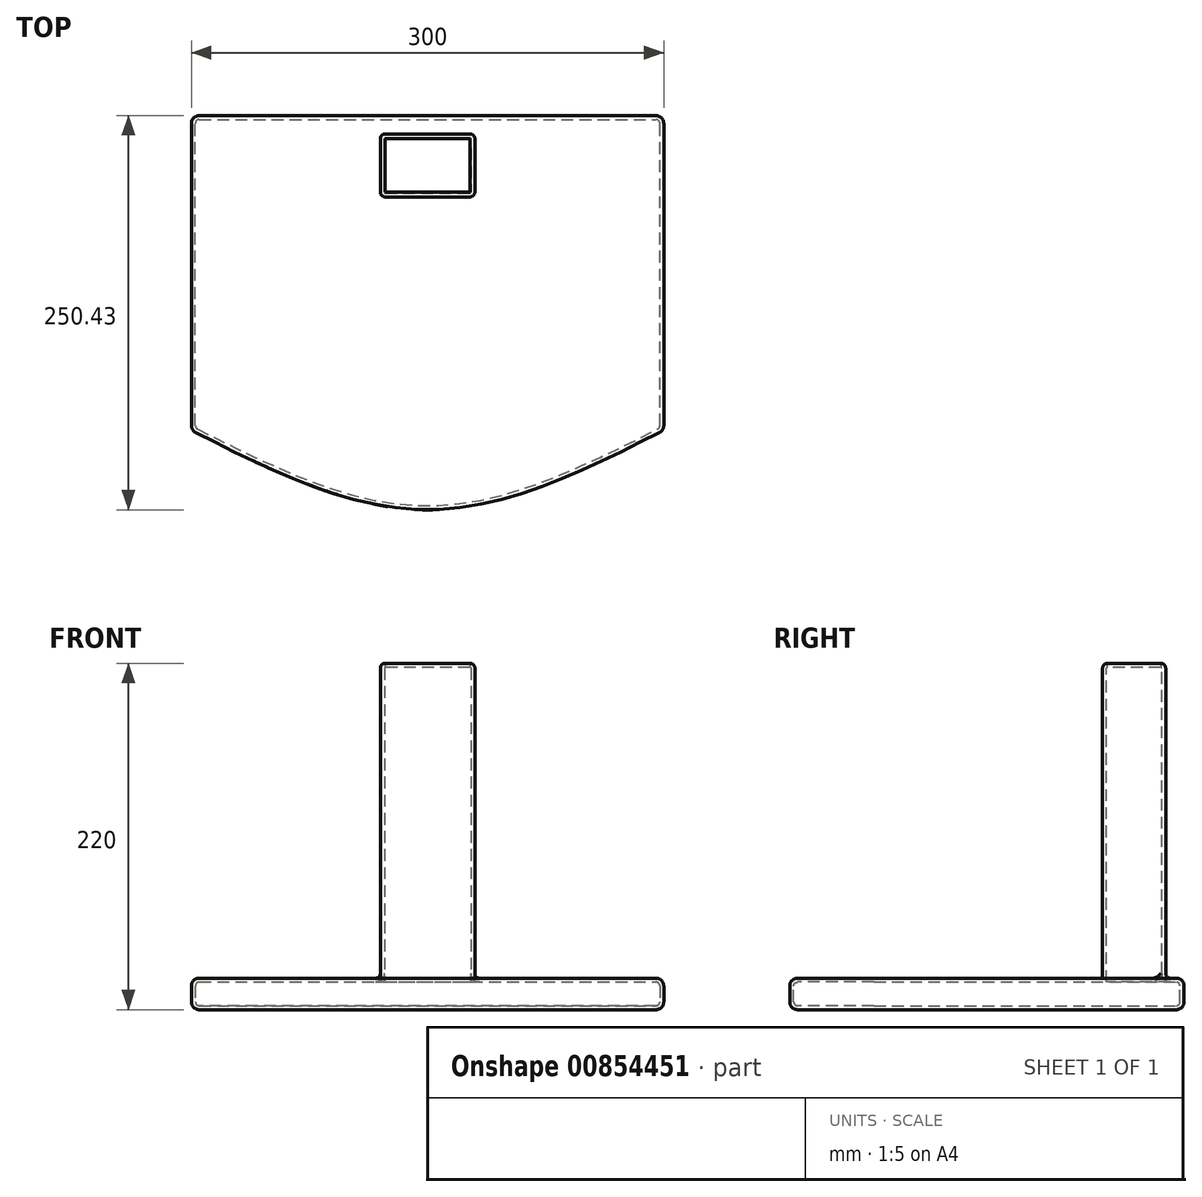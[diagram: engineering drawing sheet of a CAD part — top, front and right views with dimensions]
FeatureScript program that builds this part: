
annotation { "Feature Type Name" : "Feature", "Feature Type Description" : "" }
export const myFeature = defineFeature(function(context is Context, id is Id, definition is map)
    precondition{}
    {
        {
            var Q0;
            Q0=qCreatedBy(makeId("Top.planeOp"),FACE);
            var sketch = newSketch(context, id + "F0", { "sketchPlane" : qUnion([Q0])});
            skLineSegment(sketch, "E0.bottom", {"start": v(-150, 100) * mm, "end": v(150, 100) * mm});
            skLineSegment(sketch, "E0.left", {"start": v(-150, 100) * mm, "end": v(-150, -100) * mm});
            skLineSegment(sketch, "E0.right", {"start": v(150, 100) * mm, "end": v(150, -100) * mm});
            skFitSpline(sketch, "E1", {"points": [v(-150, -100) * mm, v(0, -150.43) * mm, v(150, -100) * mm], "startDerivative": vector(300, -151.28) * mm, "endDerivative": vector(300, 151.28) * mm});
            skSolve(sketch);
        }
        {
            var Q0;
            Q0=makeQuery(id+"F0.imprint","IMPRINT",FACE,{"disambiguationData":[TD([[makeQuery(id+"F0.imprint","IMPRINT",EDGE,{"derivedFrom":sQuery(id+"F0.wireOp",EDGE,"E0.bottom")}),-1.0]])]});
            extrude(context, id + "F1", {"entities" : qUnion([Q0]), "depth" : 20 * mm, "offsetDistance" : 25 * mm});
        }
        {
            var Q0;
            Q0=makeQuery(id+"F1.opExtrude","SWEPT_FACE",FACE,{"disambiguationData":[OSD([sQuery(id+"F0.wireOp",EDGE,"E0.left")])]});
            var Q1;
            Q1=makeQuery(id+"F1.opExtrude","SWEPT_FACE",FACE,{"disambiguationData":[OSD([sQuery(id+"F0.wireOp",EDGE,"E1")])]});
            var Q2;
            Q2=makeQuery(id+"F1.opExtrude","SWEPT_FACE",FACE,{"disambiguationData":[OSD([sQuery(id+"F0.wireOp",EDGE,"E0.right")])]});
            var Q3;
            Q3=makeQuery(id+"F1.opExtrude","SWEPT_FACE",FACE,{"disambiguationData":[OSD([sQuery(id+"F0.wireOp",EDGE,"E0.bottom")])]});
            fillet(context, id + "F2", {"entities" : qUnion([Q0, Q1, Q2, Q3]), "radius" : 5 * mm, "tangentPropagation" : true, "allowEdgeOverflow" : false});
        }
        {
            var Q0;
            Q0=makeQuery(id+"F1.opExtrude","CAP_FACE",FACE,{"disambiguationData":[OSD([sQuery(id+"F0.wireOp",EDGE,"E0.bottom"),sQuery(id+"F0.wireOp",EDGE,"E0.left"),sQuery(id+"F0.wireOp",EDGE,"E0.right"),sQuery(id+"F0.wireOp",EDGE,"E1")])],"isStart":false});
            var sketch = newSketch(context, id + "F3", { "sketchPlane" : qUnion([Q0])});
            skLineSegment(sketch, "E2.bottom", {"start": v(-30, 88.32) * mm, "end": v(30, 88.32) * mm});
            skLineSegment(sketch, "E2.top", {"start": v(-30, 48.32) * mm, "end": v(30, 48.32) * mm});
            skLineSegment(sketch, "E2.left", {"start": v(-30, 88.32) * mm, "end": v(-30, 48.32) * mm});
            skLineSegment(sketch, "E2.right", {"start": v(30, 88.32) * mm, "end": v(30, 48.32) * mm});
            skSolve(sketch);
        }
        {
            var Q0;
            Q0=makeQuery(id+"F3.imprint","IMPRINT",FACE,{"disambiguationData":[TD([[makeQuery(id+"F3.imprint","IMPRINT",EDGE,{"derivedFrom":sQuery(id+"F3.wireOp",EDGE,"E2.bottom")}),-1.0]])]});
            extrude(context, id + "F4", {"entities" : qUnion([Q0]), "operationType" : NewBodyOperationType.ADD, "depth" : 200 * mm, "offsetDistance" : 25 * mm});
        }
        {
            var Q0;
            Q0=makeQuery(id+"F4.opExtrude","CAP_EDGE",EDGE,{"disambiguationData":[OSD([sQuery(id+"F3.wireOp",EDGE,"E2.top")])],"isStart":false});
            var Q1;
            Q1=makeQuery(id+"F4.opExtrude","CAP_EDGE",EDGE,{"disambiguationData":[OSD([sQuery(id+"F3.wireOp",EDGE,"E2.right")])],"isStart":false});
            var Q2;
            Q2=makeQuery(id+"F4.opExtrude","SWEPT_EDGE",EDGE,{"disambiguationData":[OSD([sQuery(id+"F3.wireOp",EDGE,"E2.bottom"),sQuery(id+"F3.wireOp",EDGE,"E2.right")])]});
            var Q3;
            Q3=makeQuery(id+"F4.opExtrude","SWEPT_FACE",FACE,{"disambiguationData":[OSD([sQuery(id+"F3.wireOp",EDGE,"E2.bottom")])]});
            var Q4;
            Q4=makeQuery(id+"F4.opExtrude","SWEPT_EDGE",EDGE,{"disambiguationData":[OSD([sQuery(id+"F3.wireOp",EDGE,"E2.top"),sQuery(id+"F3.wireOp",EDGE,"E2.right")])]});
            var Q5;
            Q5=makeQuery(id+"F4.opExtrude","CAP_EDGE",EDGE,{"disambiguationData":[OSD([sQuery(id+"F3.wireOp",EDGE,"E2.right")])],"isStart":true});
            var Q6;
            Q6=makeQuery(id+"F4.opExtrude","SWEPT_EDGE",EDGE,{"disambiguationData":[OSD([sQuery(id+"F3.wireOp",EDGE,"E2.top"),sQuery(id+"F3.wireOp",EDGE,"E2.left")])]});
            var Q7;
            Q7=makeQuery(id+"F4.opExtrude","CAP_EDGE",EDGE,{"disambiguationData":[OSD([sQuery(id+"F3.wireOp",EDGE,"E2.left")])],"isStart":false});
            fillet(context, id + "F5", {"entities" : qUnion([Q0, Q1, Q2, Q3, Q4, Q5, Q6, Q7]), "radius" : 3 * mm, "tangentPropagation" : true, "allowEdgeOverflow" : false});
        }
        {
            var Q0;
            Q0=makeQuery(id+"F4.opExtrude","CAP_FACE",FACE,{"disambiguationData":[OSD([sQuery(id+"F3.wireOp",EDGE,"E2.bottom"),sQuery(id+"F3.wireOp",EDGE,"E2.top"),sQuery(id+"F3.wireOp",EDGE,"E2.left"),sQuery(id+"F3.wireOp",EDGE,"E2.right")])],"isStart":false});
            shell(context, id + "F6", {"entities" : qUnion([Q0]), "thickness" : 2.5 * mm});
        }
    });
